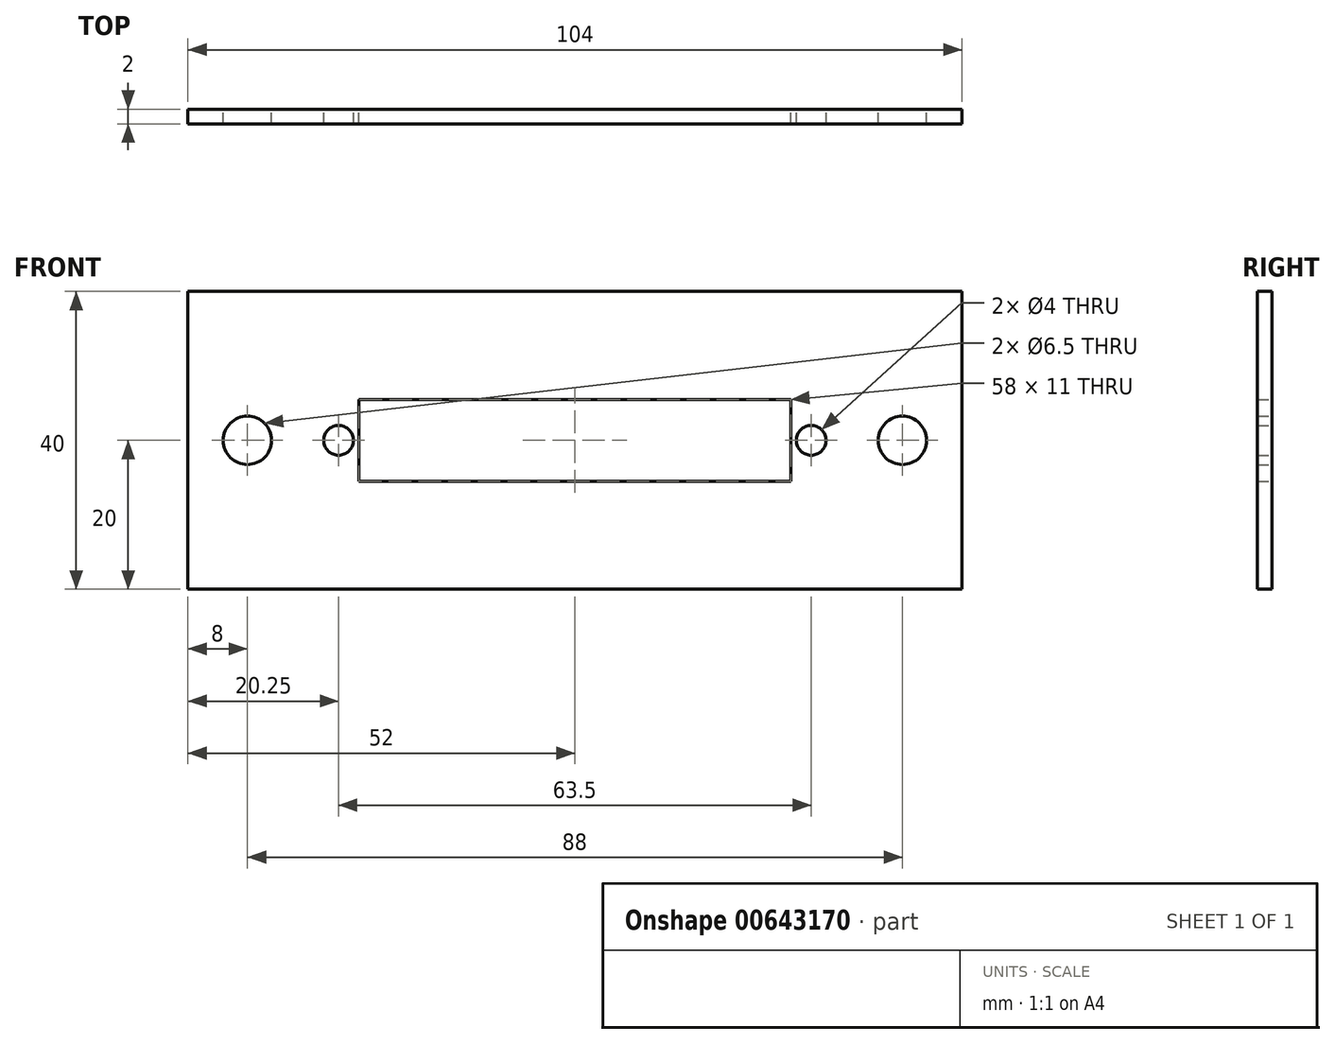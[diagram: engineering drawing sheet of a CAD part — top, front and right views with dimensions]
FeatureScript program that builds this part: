
annotation { "Feature Type Name" : "Feature", "Feature Type Description" : "" }
export const myFeature = defineFeature(function(context is Context, id is Id, definition is map)
    precondition{}
    {
        {
            var Q0;
            Q0=qCreatedBy(makeId("Front.planeOp"),FACE);
            var sketch = newSketch(context, id + "F0", { "sketchPlane" : qUnion([Q0])});
            skLineSegment(sketch, "E0.bottom", {"start": v(52, -20) * mm, "end": v(-52, -20) * mm});
            skLineSegment(sketch, "E0.top", {"start": v(52, 20) * mm, "end": v(-52, 20) * mm});
            skLineSegment(sketch, "E0.left", {"start": v(52, -20) * mm, "end": v(52, 20) * mm});
            skLineSegment(sketch, "E0.right", {"start": v(-52, -20) * mm, "end": v(-52, 20) * mm});
            skPoint(sketch, "E0.middle", {"position": v(0, 0) * mm});
            skLineSegment(sketch, "E1.bottom", {"start": v(29, -5.5) * mm, "end": v(-29, -5.5) * mm});
            skLineSegment(sketch, "E1.top", {"start": v(29, 5.5) * mm, "end": v(-29, 5.5) * mm});
            skLineSegment(sketch, "E1.left", {"start": v(29, -5.5) * mm, "end": v(29, 5.5) * mm});
            skLineSegment(sketch, "E1.right", {"start": v(-29, -5.5) * mm, "end": v(-29, 5.5) * mm});
            skCircle(sketch, "E2", {"center": v(31.75, 0) * mm, "radius": 2 * mm});
            skCircle(sketch, "E3", {"center": v(-31.75, 0) * mm, "radius": 2 * mm});
            skCircle(sketch, "E4", {"center": v(-44, 0) * mm, "radius": 3.25 * mm});
            skCircle(sketch, "E5", {"center": v(44, 0) * mm, "radius": 3.25 * mm});
            skCircle(sketch, "E6", {"center": v(-44, 0) * mm, "radius": 6 * mm, "construction": true});
            skSolve(sketch);
        }
        {
            var Q0;
            Q0=makeQuery(id+"F0.imprint","IMPRINT",FACE,{"disambiguationData":[TD([[makeQuery(id+"F0.imprint","IMPRINT",EDGE,{"derivedFrom":sQuery(id+"F0.wireOp",EDGE,"E0.bottom")}),-1.0]])]});
            extrude(context, id + "F1", {"entities" : qUnion([Q0]), "depth" : 2 * mm, "offsetDistance" : 25 * mm});
        }
    });
